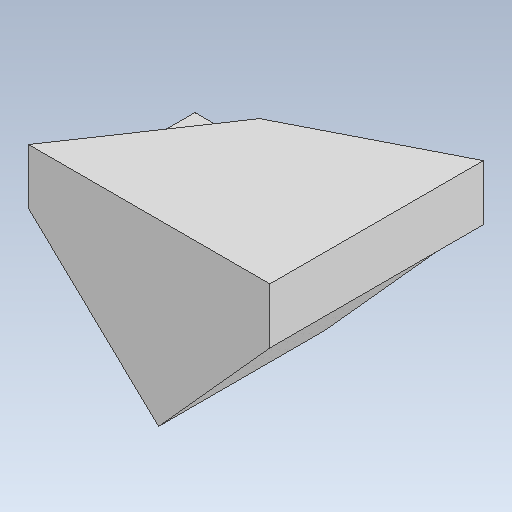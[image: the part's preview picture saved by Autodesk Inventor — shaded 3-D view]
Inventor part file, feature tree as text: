
AUTODESK INVENTOR PART (.ipt)
format: ipt  version: 2021 (Build 250183000, 183)  size: 113,152 bytes
history: native  units: mm
features: extrude x2, sketch x2
ambient origin geometry x8: Origin, YZ Plane, XZ Plane, XY Plane, X Axis, Y Axis, Z Axis, Center Point
bodies: Solid1 (feature_tree)
feature tree (4):
  extrude  "Extrusion1"  Depth=30.0mm
  extrude  "Extrusion2"  Depth=10.0mm TaperAngle=0.0deg
  sketch  "Sketch1"  dims[d0=9.773844mm d2=30.0mm]
  sketch  "Sketch2"  dims[d3=30.0mm d4=10.0mm d5=0.0mm d6=8.37758mm d7=30.0mm d8=30.0mm d9=0.0mm d10=4.712389mm]
